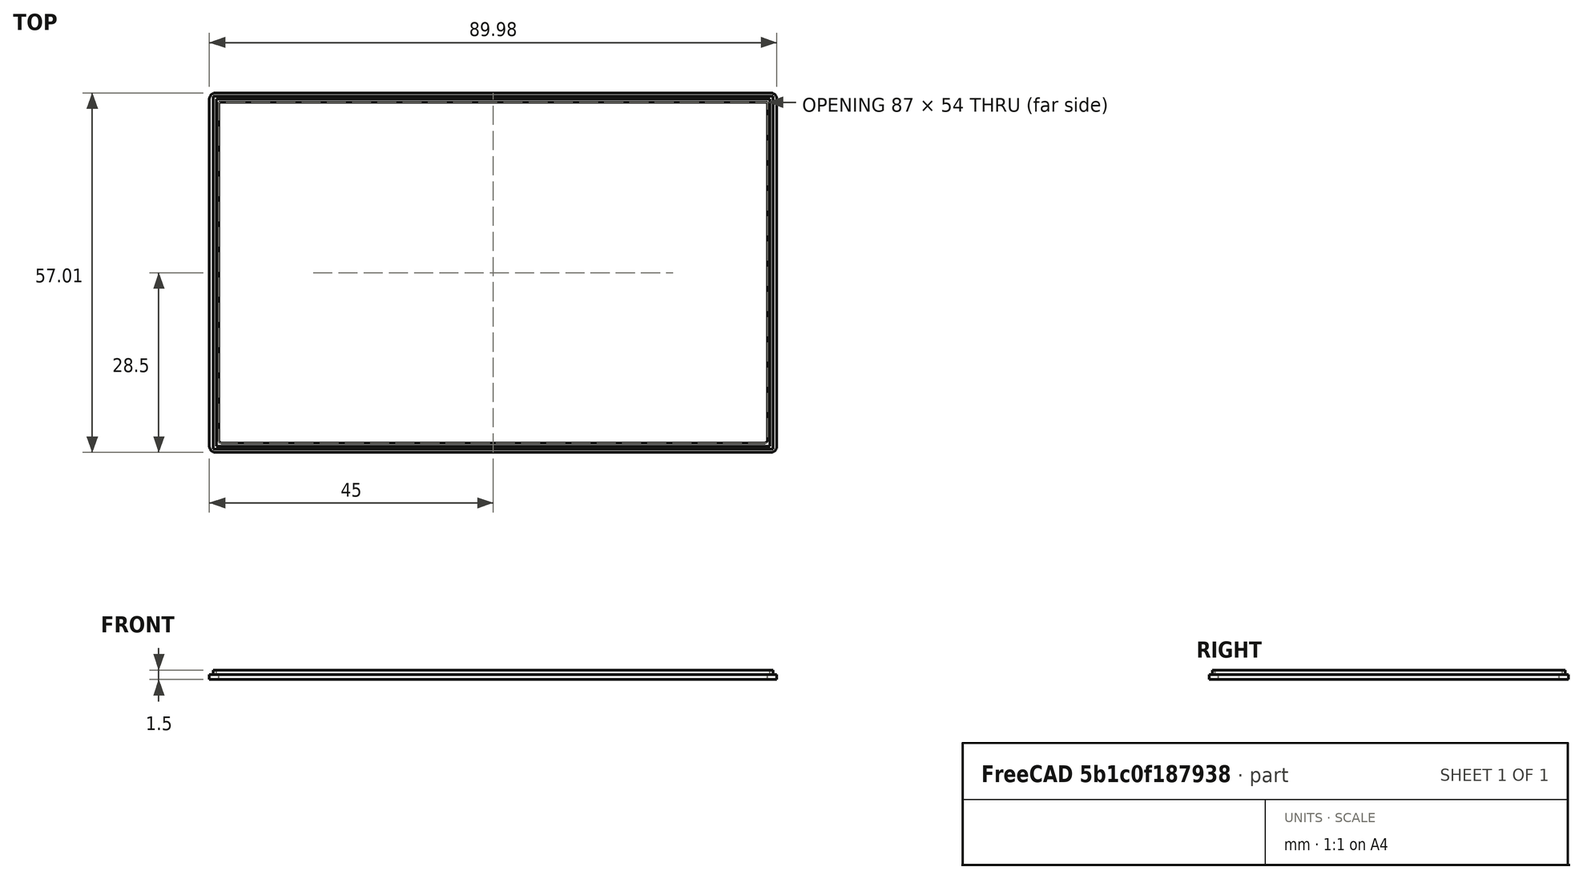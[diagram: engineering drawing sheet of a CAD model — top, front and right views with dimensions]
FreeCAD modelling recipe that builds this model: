
FCSTD DOCUMENT  (FreeCAD 0.18.4R)
Label: BoxGasket3
License: All rights reserved
LicenseURL: http://en.wikipedia.org/wiki/All_rights_reserved
objects: Part::Box×3, Part::Cut×2, Sketcher::SketchObject×1, PartDesign::Pad×1, Part::Fillet×1, Part::MultiFuse×1, Mesh::Feature×1
note: 10 computed .brp shape members not serialized (recipe doc carries the construction recipe); baked Part::Feature solids carry a one-line shape summary decoded from their .brp

FEATURE [Sketcher::SketchObject] Sketch002
  MapMode = 5
  sketch-geometry (8):
    g0: LineSegment StartX=16.0115 StartY=-28 StartZ=0 EndX=-72 EndY=-28 EndZ=0
    g1: LineSegment StartX=-73.0008 StartY=-26.9992 StartZ=0 EndX=-73.0008 EndY=28.0015 EndZ=0
    g2: LineSegment StartX=-71.9972 StartY=29.005 StartZ=0 EndX=15.9984 EndY=29.005 EndZ=0
    g3: LineSegment StartX=16.9833 StartY=28.0201 StartZ=0 EndX=16.9833 EndY=-27.0282 EndZ=0
    g4: ArcOfCircle CenterX=16.0115 CenterY=-27.0282 CenterZ=0 NormalX=0 NormalY=0 NormalZ=1 AngleXU=0 Radius=0.97176 StartAngle=4.71239 EndAngle=6.28319
    g5: ArcOfCircle CenterX=-72 CenterY=-26.9992 CenterZ=0 NormalX=0 NormalY=0 NormalZ=1 AngleXU=0 Radius=1.00077 StartAngle=3.14159 EndAngle=4.71239
    g6: ArcOfCircle CenterX=-71.9972 CenterY=28.0015 CenterZ=0 NormalX=0 NormalY=0 NormalZ=1 AngleXU=0 Radius=1.00354 StartAngle=1.5708 EndAngle=3.14159
    g7: ArcOfCircle CenterX=15.9984 CenterY=28.0201 CenterZ=0 NormalX=0 NormalY=0 NormalZ=1 AngleXU=0 Radius=0.984903 StartAngle=0 EndAngle=1.5708
  constraints (12):
    c: Horizontal(g0)
    c: Horizontal(g2)
    c: Vertical(g1)
    c: Vertical(g3)
    c: Tangent(g3,g4) = 1.5708
    c: Tangent(g0,g4) = 1.5708
    c: Tangent(g1,g5) = 1.5708
    c: Tangent(g0,g5) = 1.5708
    c: Tangent(g1,g6) = 1.5708
    c: Tangent(g2,g6) = 1.5708
    c: Tangent(g2,g7) = 1.5708
    c: Tangent(g3,g7) = 1.5708
FEATURE [PartDesign::Pad] Pad013
  Length = 0.75
  Length2 = 100
  Profile = -> Sketch002
  Type = 0
FEATURE [Part::Box] Box010  label="Würfel010"
  AttacherType = Attacher::AttachEngine3D
  Height = 3
  Length = 87
  Placement = pos=(-71.5,-26.5,-1) rot=(0,0,1;0rad)
  Width = 54
FEATURE [Part::Cut] Cut
  Base = -> Pad013
  Tool = -> Box010
FEATURE [Part::Fillet] Fillet
  Base = -> Cut
  Edges = 2 edges r=0.5: [Edge35,Edge36]
FEATURE [Part::Box] Box  label="Würfel"
  AttacherType = Attacher::AttachEngine3D
  Height = 1
  Length = 88.8
  Placement = pos=(-72.4,-27.5,1) rot=(0,0,1;0rad)
  Width = 56
FEATURE [Part::Box] Box011  label="Würfel011"
  AttacherType = Attacher::AttachEngine3D
  Height = 2
  Length = 87.8
  Placement = pos=(-71.9,-27,0.5) rot=(0,0,1;0rad)
  Width = 55
FEATURE [Part::Cut] Cut001
  Base = -> Box
  Placement = pos=(0,0,-0.5) rot=(0,0,1;0rad)
  Tool = -> Box011
FEATURE [Part::MultiFuse] Fusion
  Shapes = -> [Fillet,Cut001]
FEATURE [Mesh::Feature] Mesh  label="Fusion (Meshed)"
